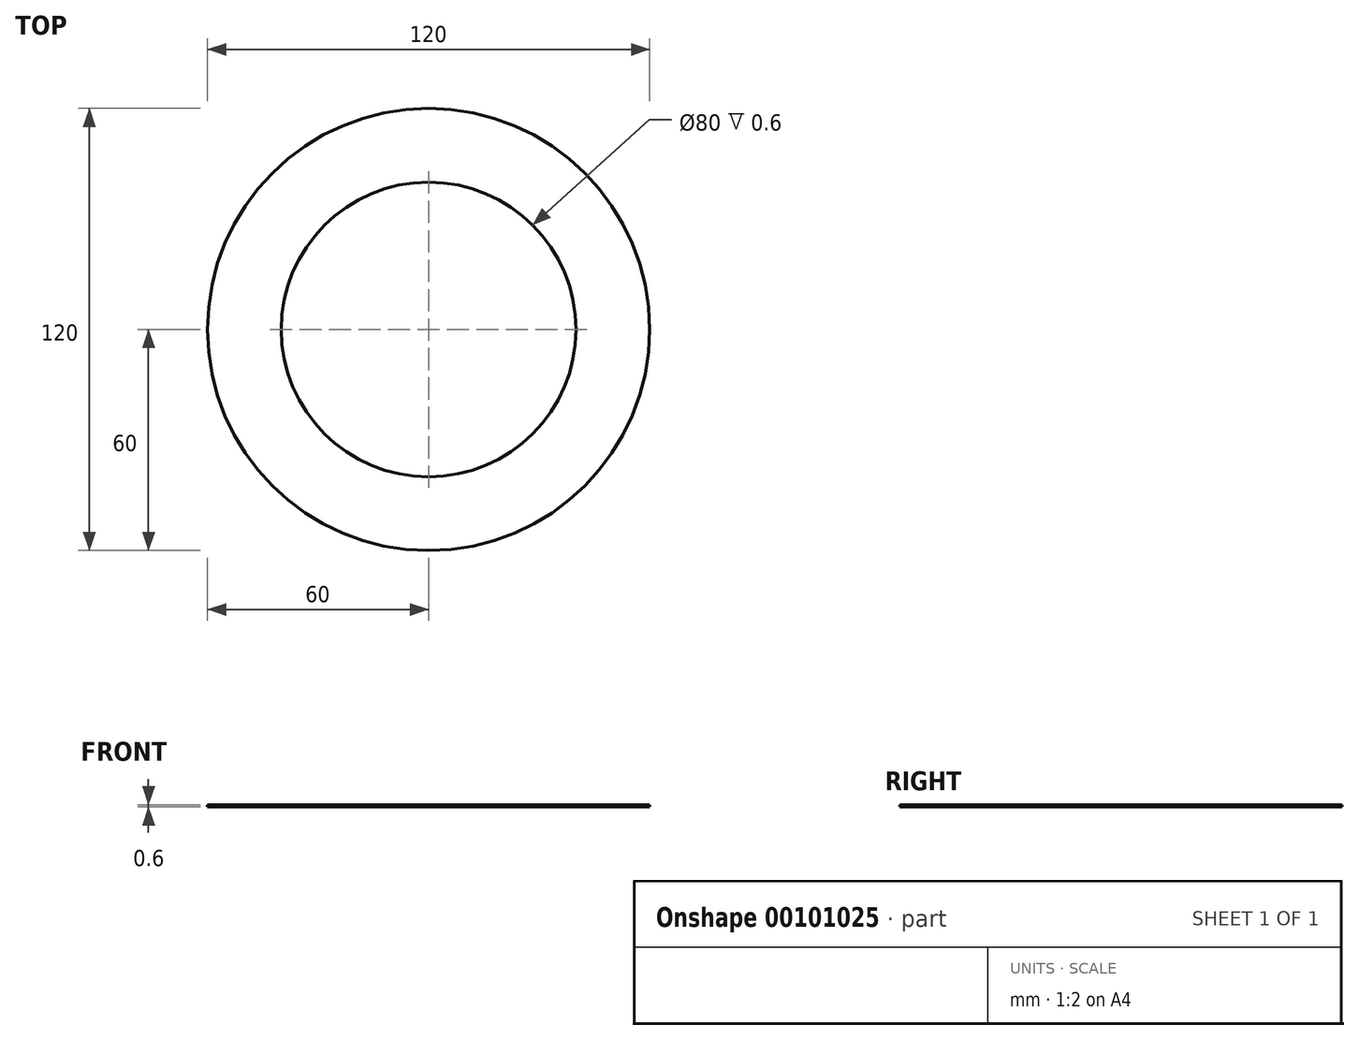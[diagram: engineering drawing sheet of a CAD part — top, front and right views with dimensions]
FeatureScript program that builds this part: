
annotation { "Feature Type Name" : "Feature", "Feature Type Description" : "" }
export const myFeature = defineFeature(function(context is Context, id is Id, definition is map)
    precondition{}
    {
        {
            var Q0;
            Q0=qCreatedBy(makeId("Front.planeOp"),FACE);
            var sketch = newSketch(context, id + "F0", { "sketchPlane" : qUnion([Q0])});
            skLineSegment(sketch, "E0.bottom", {"start": v(-60, 0) * mm, "end": v(-40, 0) * mm});
            skLineSegment(sketch, "E0.top", {"start": v(-60, 0.6) * mm, "end": v(-40, 0.6) * mm});
            skLineSegment(sketch, "E0.left", {"start": v(-60, 0) * mm, "end": v(-60, 0.6) * mm});
            skLineSegment(sketch, "E0.right", {"start": v(-40, 0) * mm, "end": v(-40, 0.6) * mm});
            skLineSegment(sketch, "E1.bottom", {"start": v(-50.24, 0.6) * mm, "end": v(-49.76, 0.6) * mm});
            skLineSegment(sketch, "E1.top", {"start": v(-50.24, 50.6) * mm, "end": v(-49.76, 50.6) * mm});
            skLineSegment(sketch, "E1.left", {"start": v(-50.24, 0.6) * mm, "end": v(-50.24, 50.6) * mm});
            skLineSegment(sketch, "E1.right", {"start": v(-49.76, 0.6) * mm, "end": v(-49.76, 50.6) * mm});
            skPoint(sketch, "E2", {"position": v(-50, 0.6) * mm});
            skLineSegment(sketch, "E3", {"start": v(0, 0) * mm, "end": v(0, 51.73) * mm, "construction": true});
            skSolve(sketch);
        }
        {
            var Q0;
            Q0=makeQuery(id+"F0.imprint","IMPRINT",FACE,{"disambiguationData":[TD([[makeQuery(id+"F0.imprint","IMPRINT",EDGE,{"derivedFrom":sQuery(id+"F0.wireOp",EDGE,"E0.bottom")}),1.0]])]});
            var Q1;
            Q1=makeQuery(id+"F0.imprint","IMPRINT",FACE,{"disambiguationData":[TD([[makeQuery(id+"F0.imprint","IMPRINT",EDGE,{"derivedFrom":sQuery(id+"F0.wireOp",EDGE,"E1.bottom")}),1.0]])]});
            var Q2;
            Q2=sQuery(id+"F0.wireOp",EDGE,"E3");
            revolve(context, id + "F1", {"entities" : qUnion([Q0, Q1]), "axis" : qUnion([Q2]), "revolveType" : RevolveType.FULL});
        }
    });
